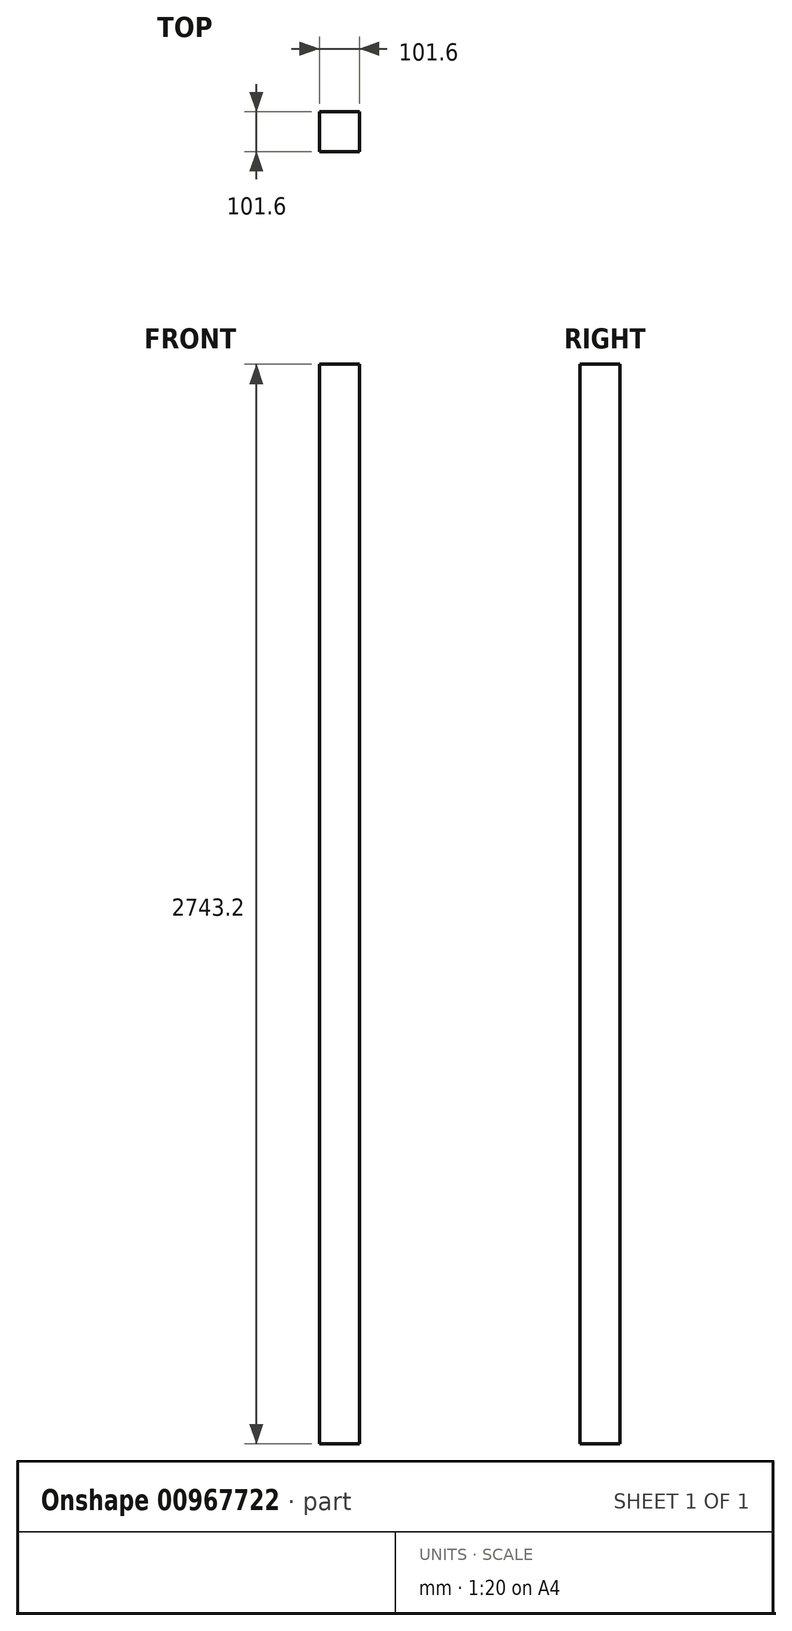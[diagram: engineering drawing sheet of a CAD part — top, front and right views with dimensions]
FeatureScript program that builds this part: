
annotation { "Feature Type Name" : "Feature", "Feature Type Description" : "" }
export const myFeature = defineFeature(function(context is Context, id is Id, definition is map)
    precondition{}
    {
        {
            var Q0;
            Q0=qCreatedBy(makeId("Top.planeOp"),FACE);
            var sketch = newSketch(context, id + "F0", { "sketchPlane" : qUnion([Q0])});
            skLineSegment(sketch, "E0.bottom", {"start": v(50.8, 50.8) * mm, "end": v(-50.8, 50.8) * mm});
            skLineSegment(sketch, "E0.top", {"start": v(50.8, -50.8) * mm, "end": v(-50.8, -50.8) * mm});
            skLineSegment(sketch, "E0.left", {"start": v(50.8, 50.8) * mm, "end": v(50.8, -50.8) * mm});
            skLineSegment(sketch, "E0.right", {"start": v(-50.8, 50.8) * mm, "end": v(-50.8, -50.8) * mm});
            skPoint(sketch, "E0.middle", {"position": v(0, 0) * mm});
            skSolve(sketch);
        }
        {
            var Q0;
            Q0 = qSketchRegion(id + "F0", true);
            extrude(context, id + "F1", {"entities" : qUnion([Q0]), "depth" : 2743.2 * mm, "offsetDistance" : 25.4 * mm});
        }
    });
